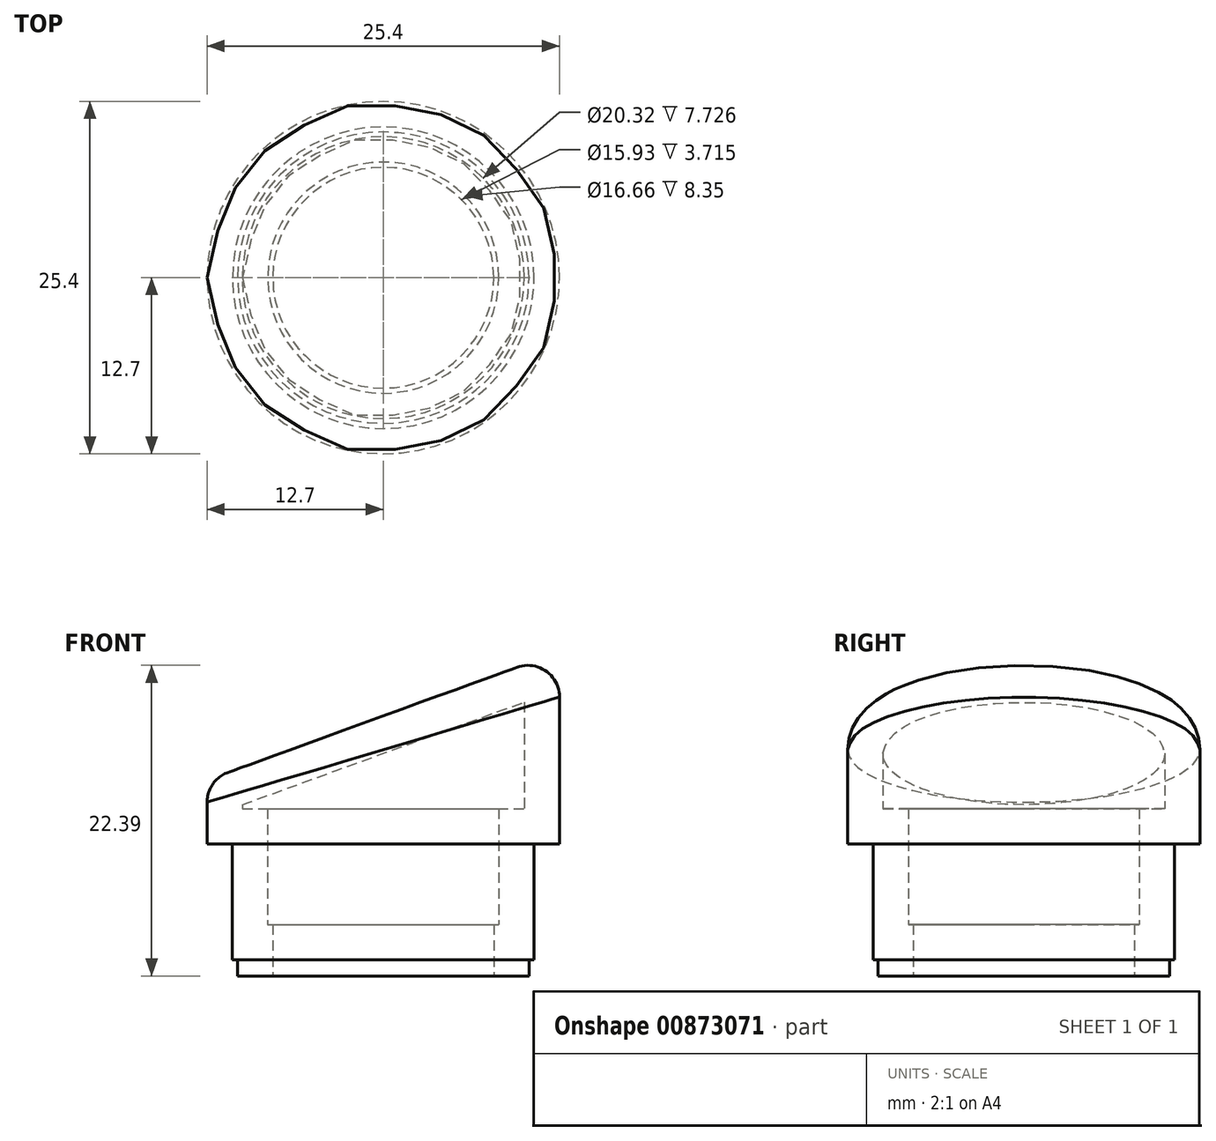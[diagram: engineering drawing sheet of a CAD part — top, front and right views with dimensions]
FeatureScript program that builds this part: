
annotation { "Feature Type Name" : "Feature", "Feature Type Description" : "" }
export const myFeature = defineFeature(function(context is Context, id is Id, definition is map)
    precondition{}
    {
        {
            var Q0;
            Q0=qCreatedBy(makeId("Front.planeOp"),FACE);
            var sketch = newSketch(context, id + "F0", { "sketchPlane" : qUnion([Q0])});
            skLineSegment(sketch, "E0", {"start": v(0, 0) * mm, "end": v(0, 23.37) * mm});
            skLineSegment(sketch, "E1", {"start": v(0, 0) * mm, "end": v(10.5, 0) * mm});
            skLineSegment(sketch, "E2", {"start": v(12.7, 23.37) * mm, "end": v(12.7, 9.53) * mm});
            skLineSegment(sketch, "E3", {"start": v(10.87, 1.17) * mm, "end": v(10.87, 9.53) * mm});
            skLineSegment(sketch, "E4", {"start": v(10.87, 9.53) * mm, "end": v(12.7, 9.53) * mm});
            skLineSegment(sketch, "E5", {"start": v(10.5, 0) * mm, "end": v(10.5, 1.17) * mm});
            skLineSegment(sketch, "E6", {"start": v(10.5, 1.17) * mm, "end": v(10.87, 1.17) * mm});
            skLineSegment(sketch, "E7", {"start": v(12.7, 23.37) * mm, "end": v(0, 23.37) * mm});
            skSolve(sketch);
        }
        {
            var Q0;
            Q0=makeQuery(id+"F0.imprint","IMPRINT",FACE,{"disambiguationData":[TD([[makeQuery(id+"F0.imprint","IMPRINT",EDGE,{"derivedFrom":sQuery(id+"F0.wireOp",EDGE,"E0")}),-1.0]])]});
            var Q1;
            Q1=sQuery(id+"F0.wireOp",EDGE,"E0");
            revolve(context, id + "F1", {"surfaceOperationType" : NewSurfaceOperationType.NEW, "entities" : qUnion([Q0]), "axis" : qUnion([Q1]), "revolveType" : RevolveType.FULL});
        }
        {
            var Q0;
            Q0=qCreatedBy(makeId("Front.planeOp"),FACE);
            var sketch = newSketch(context, id + "F2", { "sketchPlane" : qUnion([Q0])});
            skLineSegment(sketch, "E8.0", {"start": v(12.7, 23.37) * mm, "end": v(-21.73, 23.37) * mm});
            skLineSegment(sketch, "E9", {"start": v(12.7, 23.37) * mm, "end": v(-21.73, 10.84) * mm});
            skLineSegment(sketch, "E10", {"start": v(-21.73, 10.84) * mm, "end": v(-21.73, 23.37) * mm});
            skPoint(sketch, "E11.orphan", {"position": v(-12.7, 23.37) * mm});
            skSolve(sketch);
        }
        {
            var Q0;
            Q0=makeQuery(id+"F2.imprint","IMPRINT",FACE,{"disambiguationData":[TD([[makeQuery(id+"F2.imprint","IMPRINT",EDGE,{"derivedFrom":sQuery(id+"F2.wireOp",EDGE,"E8.0")}),1.0]])]});
            extrude(context, id + "F3", {"entities" : qUnion([Q0]), "operationType" : NewBodyOperationType.REMOVE, "endBound" : BoundingType.SYMMETRIC, "oppositeDirection" : true, "depth" : 25.4 * mm, "offsetDistance" : 25.4 * mm});
        }
        {
            var Q0;
            Q0=makeQuery(id+"F3.boolean.opBoolean","INTERSECT",EDGE,{"derivedFrom":[makeQuery(id+"F1.opRevolve","SWEPT_FACE",FACE,{"disambiguationData":[OSD([sQuery(id+"F0.wireOp",EDGE,"E2")])]}),makeQuery(id+"F3.opExtrude","SWEPT_FACE",FACE,{"disambiguationData":[OSD([sQuery(id+"F2.wireOp",EDGE,"E9")])]})]});
            fillet(context, id + "F4", {"entities" : qUnion([Q0]), "radius" : 2.3 * mm, "tangentPropagation" : true, "allowEdgeOverflow" : false});
        }
        {
            var Q0;
            Q0=makeQuery(id+"F1.opRevolve","SWEPT_FACE",FACE,{"disambiguationData":[OSD([sQuery(id+"F0.wireOp",EDGE,"E1")])]});
            shell(context, id + "F5", {"entities" : qUnion([Q0]), "thickness" : 2.54 * mm});
        }
    });
